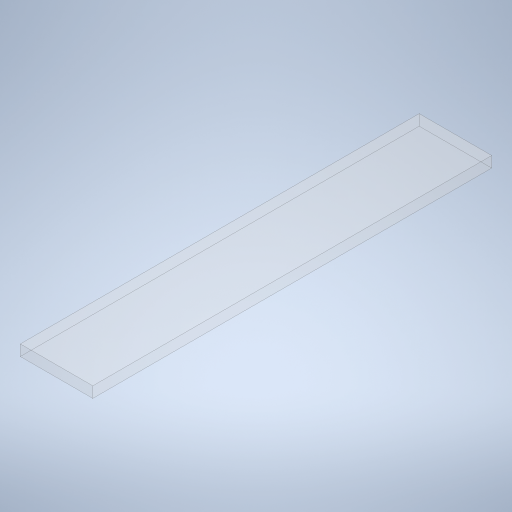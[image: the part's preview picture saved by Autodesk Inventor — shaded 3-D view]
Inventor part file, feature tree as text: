
AUTODESK INVENTOR PART (.ipt)
format: ipt  version: 2024 (Build 280153000, 153)  size: 241,664 bytes
history: native  units: mm
features: other x1, extrude x1, sketch x1
ambient origin geometry x8: Origin, YZ Plane, XZ Plane, XY Plane, X Axis, Y Axis, Z Axis, Center Point
bodies: Body1 (feature_tree)
feature tree (3):
  other  "솔리드1"
  extrude  "돌출1"  Depth=20.0mm
  sketch  "스케치1"
